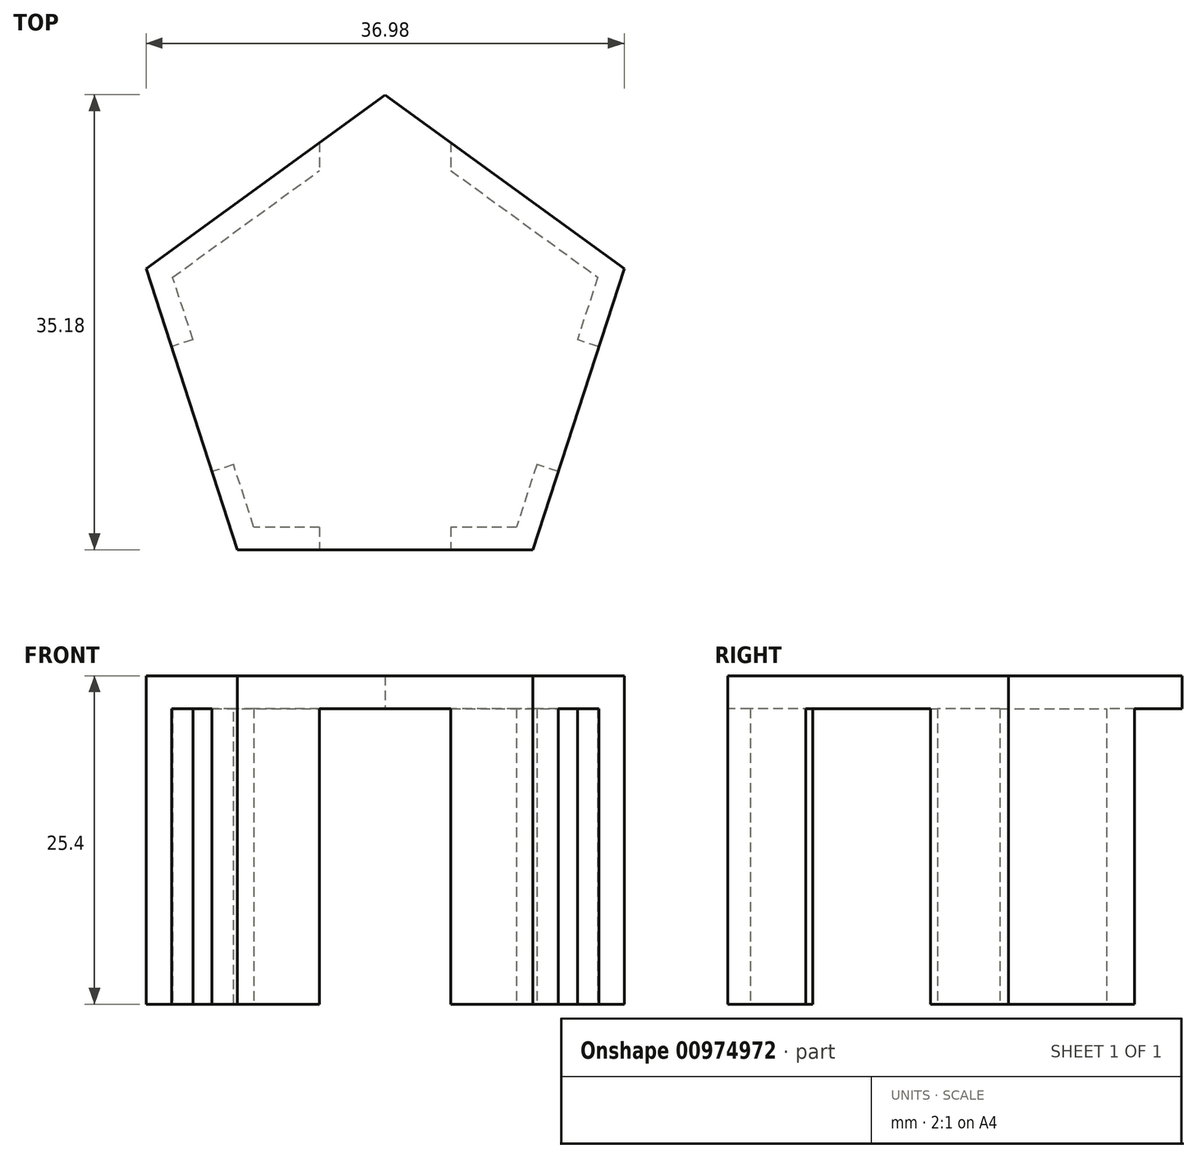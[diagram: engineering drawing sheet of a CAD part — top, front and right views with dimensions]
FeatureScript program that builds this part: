
annotation { "Feature Type Name" : "Feature", "Feature Type Description" : "" }
export const myFeature = defineFeature(function(context is Context, id is Id, definition is map)
    precondition{}
    {
        {
            var Q0;
            Q0=qCreatedBy(makeId("Top.planeOp"),FACE);
            var sketch = newSketch(context, id + "F0", { "sketchPlane" : qUnion([Q0])});
            skCircle(sketch, "E0.cCircle", {"center": v(0, 0) * mm, "radius": 19.45 * mm, "construction": true});
            skLineSegment(sketch, "E0.0", {"start": v(11.43, -15.73) * mm, "end": v(-11.43, -15.73) * mm});
            skLineSegment(sketch, "E0.1", {"start": v(-11.43, -15.73) * mm, "end": v(-18.5, 6) * mm});
            skLineSegment(sketch, "E0.2", {"start": v(-18.5, 6) * mm, "end": v(0, 19.45) * mm});
            skLineSegment(sketch, "E0.3", {"start": v(0, 19.45) * mm, "end": v(18.5, 6) * mm});
            skLineSegment(sketch, "E0.4", {"start": v(18.5, 6) * mm, "end": v(11.43, -15.73) * mm});
            skSolve(sketch);
        }
        {
            var Q0;
            Q0=makeQuery(id+"F0.imprint","IMPRINT",FACE,{"disambiguationData":[TD([[makeQuery(id+"F0.imprint","IMPRINT",EDGE,{"derivedFrom":sQuery(id+"F0.wireOp",EDGE,"E0.0")}),-1.0]])]});
            extrude(context, id + "F1", {"entities" : qUnion([Q0]), "depth" : 25.4 * mm, "offsetDistance" : 25.4 * mm});
        }
        {
            var Q0;
            Q0=qCreatedBy(makeId("Top.planeOp"),FACE);
            var sketch = newSketch(context, id + "F2", { "sketchPlane" : qUnion([Q0])});
            skCircle(sketch, "E1.cCircle", {"center": v(0, 0) * mm, "radius": 13.98 * mm, "construction": true});
            skLineSegment(sketch, "E1.0", {"start": v(16.44, 5.34) * mm, "end": v(10.16, -13.98) * mm});
            skLineSegment(sketch, "E1.1", {"start": v(10.16, -13.98) * mm, "end": v(-10.16, -13.98) * mm});
            skLineSegment(sketch, "E1.2", {"start": v(-10.16, -13.98) * mm, "end": v(-16.44, 5.34) * mm});
            skLineSegment(sketch, "E1.3", {"start": v(-16.44, 5.34) * mm, "end": v(0, 17.29) * mm});
            skLineSegment(sketch, "E1.4", {"start": v(0, 17.29) * mm, "end": v(16.44, 5.34) * mm});
            skPoint(sketch, "E1.0.midPoint", {"position": v(13.3, -4.32) * mm});
            skSolve(sketch);
        }
        {
            var Q0;
            Q0 = qSketchRegion(id + "F2", true);
            extrude(context, id + "F3", {"entities" : qUnion([Q0]), "operationType" : NewBodyOperationType.REMOVE, "depth" : 22.86 * mm, "offsetDistance" : 25.4 * mm});
        }
        {
            var Q0;
            Q0=makeQuery(id+"F1.opExtrude","CAP_FACE",FACE,{"disambiguationData":[OSD([sQuery(id+"F0.wireOp",EDGE,"E0.0"),sQuery(id+"F0.wireOp",EDGE,"E0.1"),sQuery(id+"F0.wireOp",EDGE,"E0.2"),sQuery(id+"F0.wireOp",EDGE,"E0.3"),sQuery(id+"F0.wireOp",EDGE,"E0.4")])],"isStart":true});
            var sketch = newSketch(context, id + "F4", { "sketchPlane" : qUnion([Q0])});
            skLineSegment(sketch, "E2", {"start": v(0, 0) * mm, "end": v(23.62, 7.67) * mm});
            skLineSegment(sketch, "E3", {"start": v(0, 0) * mm, "end": v(-35.57, 11.56) * mm});
            skLineSegment(sketch, "E4", {"start": v(0, 0) * mm, "end": v(0, -28.1) * mm});
            skLineSegment(sketch, "E5.bottom", {"start": v(-11.25, -1.69) * mm, "end": v(-18.5, 0.67) * mm});
            skLineSegment(sketch, "E5.top", {"start": v(-8.1, 7.98) * mm, "end": v(-15.35, 10.33) * mm});
            skLineSegment(sketch, "E5.left", {"start": v(-11.25, -1.69) * mm, "end": v(-8.1, 7.98) * mm});
            skLineSegment(sketch, "E5.right", {"start": v(-18.5, 0.67) * mm, "end": v(-15.35, 10.33) * mm});
            skPoint(sketch, "E5.middle", {"position": v(-13.3, 4.32) * mm});
            skLineSegment(sketch, "E6.bottom", {"start": v(18.5, 0.67) * mm, "end": v(11.25, -1.69) * mm});
            skLineSegment(sketch, "E6.top", {"start": v(15.35, 10.33) * mm, "end": v(8.1, 7.98) * mm});
            skLineSegment(sketch, "E6.left", {"start": v(18.5, 0.67) * mm, "end": v(15.35, 10.33) * mm});
            skLineSegment(sketch, "E6.right", {"start": v(11.25, -1.69) * mm, "end": v(8.1, 7.98) * mm});
            skPoint(sketch, "E6.middle", {"position": v(13.3, 4.32) * mm});
            skLineSegment(sketch, "E7.bottom", {"start": v(5.08, -22.37) * mm, "end": v(-5.08, -22.37) * mm});
            skLineSegment(sketch, "E7.top", {"start": v(5.08, -12.2) * mm, "end": v(-5.08, -12.2) * mm});
            skLineSegment(sketch, "E7.left", {"start": v(5.08, -22.37) * mm, "end": v(5.08, -12.2) * mm});
            skLineSegment(sketch, "E7.right", {"start": v(-5.08, -22.37) * mm, "end": v(-5.08, -12.2) * mm});
            skPoint(sketch, "E7.middle", {"position": v(0, -17.29) * mm});
            skLineSegment(sketch, "E8.bottom", {"start": v(5.08, 10.17) * mm, "end": v(-5.08, 10.17) * mm});
            skLineSegment(sketch, "E8.top", {"start": v(5.08, 17.8) * mm, "end": v(-5.08, 17.8) * mm});
            skLineSegment(sketch, "E8.left", {"start": v(5.08, 10.17) * mm, "end": v(5.08, 17.8) * mm});
            skLineSegment(sketch, "E8.right", {"start": v(-5.08, 10.17) * mm, "end": v(-5.08, 17.8) * mm});
            skPoint(sketch, "E8.middle", {"position": v(0, 13.98) * mm});
            skSolve(sketch);
        }
        {
            var Q0;
            {var subQ0=sQuery(id+"F4.wireOp",EDGE,"E3");var subQ1=makeQuery(id+"F3.boolean.opBoolean","COPY",EDGE,{"derivedFrom":makeQuery(id+"F3.opExtrude","CAP_EDGE",EDGE,{"disambiguationData":[OSD([sQuery(id+"F2.wireOp",EDGE,"E1.2")])],"isStart":true})});var subQ2=makeQuery(id+"F4.imprint","INTERSECT",VERTEX,{"derivedFrom":[subQ1,subQ0]});Q0=makeQuery(id+"F4.imprint","IMPRINT",FACE,{"disambiguationData":[TD([[makeQuery(id+"F4.imprint","IMPRINT",EDGE,{"disambiguationData":[TD([[subQ2,-1.0]])],"derivedFrom":subQ0}),1.0]])]});}
            var Q1;
            {var subQ0=sQuery(id+"F4.wireOp",EDGE,"E3");var subQ1=makeQuery(id+"F3.boolean.opBoolean","COPY",EDGE,{"derivedFrom":makeQuery(id+"F3.opExtrude","CAP_EDGE",EDGE,{"disambiguationData":[OSD([sQuery(id+"F2.wireOp",EDGE,"E1.2")])],"isStart":true})});var subQ2=makeQuery(id+"F4.imprint","INTERSECT",VERTEX,{"derivedFrom":[subQ1,subQ0]});Q1=makeQuery(id+"F4.imprint","IMPRINT",FACE,{"disambiguationData":[TD([[makeQuery(id+"F4.imprint","IMPRINT",EDGE,{"disambiguationData":[TD([[subQ2,-1.0]])],"derivedFrom":subQ0}),-1.0]])]});}
            var Q2;
            {var subQ0=sQuery(id+"F4.wireOp",EDGE,"E2");var subQ1=makeQuery(id+"F3.boolean.opBoolean","COPY",EDGE,{"derivedFrom":makeQuery(id+"F3.opExtrude","CAP_EDGE",EDGE,{"disambiguationData":[OSD([sQuery(id+"F2.wireOp",EDGE,"E1.0")])],"isStart":true})});var subQ2=makeQuery(id+"F4.imprint","INTERSECT",VERTEX,{"derivedFrom":[subQ1,subQ0]});Q2=makeQuery(id+"F4.imprint","IMPRINT",FACE,{"disambiguationData":[TD([[makeQuery(id+"F4.imprint","IMPRINT",EDGE,{"disambiguationData":[TD([[subQ2,-1.0]])],"derivedFrom":subQ0}),1.0]])]});}
            var Q3;
            {var subQ0=sQuery(id+"F4.wireOp",EDGE,"E2");var subQ1=makeQuery(id+"F3.boolean.opBoolean","COPY",EDGE,{"derivedFrom":makeQuery(id+"F3.opExtrude","CAP_EDGE",EDGE,{"disambiguationData":[OSD([sQuery(id+"F2.wireOp",EDGE,"E1.0")])],"isStart":true})});var subQ2=makeQuery(id+"F4.imprint","INTERSECT",VERTEX,{"derivedFrom":[subQ1,subQ0]});Q3=makeQuery(id+"F4.imprint","IMPRINT",FACE,{"disambiguationData":[TD([[makeQuery(id+"F4.imprint","IMPRINT",EDGE,{"disambiguationData":[TD([[subQ2,-1.0]])],"derivedFrom":subQ0}),-1.0]])]});}
            var Q4;
            {var subQ1=makeQuery(id+"F1.opExtrude","CAP_EDGE",EDGE,{"disambiguationData":[OSD([sQuery(id+"F0.wireOp",EDGE,"E0.2")])],"isStart":true});var subQ5=sQuery(id+"F4.wireOp",EDGE,"E7.right");var subQ6=makeQuery(id+"F4.imprint","INTERSECT",VERTEX,{"derivedFrom":[subQ1,subQ5]});Q4=makeQuery(id+"F4.imprint","IMPRINT",FACE,{"disambiguationData":[TD([[makeQuery(id+"F4.imprint","IMPRINT",EDGE,{"disambiguationData":[TD([[subQ6,-1.0]])],"derivedFrom":subQ5}),-1.0]])]});}
            var Q5;
            {var subQ1=makeQuery(id+"F1.opExtrude","CAP_EDGE",EDGE,{"disambiguationData":[OSD([sQuery(id+"F0.wireOp",EDGE,"E0.3")])],"isStart":true});var subQ5=sQuery(id+"F4.wireOp",EDGE,"E7.left");var subQ6=makeQuery(id+"F4.imprint","INTERSECT",VERTEX,{"derivedFrom":[subQ1,subQ5]});Q5=makeQuery(id+"F4.imprint","IMPRINT",FACE,{"disambiguationData":[TD([[makeQuery(id+"F4.imprint","IMPRINT",EDGE,{"disambiguationData":[TD([[subQ6,-1.0]])],"derivedFrom":subQ5}),1.0]])]});}
            var Q6;
            {var subQ0=sQuery(id+"F4.wireOp",EDGE,"E8.left");var subQ1=makeQuery(id+"F1.opExtrude","CAP_EDGE",EDGE,{"disambiguationData":[OSD([sQuery(id+"F0.wireOp",EDGE,"E0.0")])],"isStart":true});var subQ2=makeQuery(id+"F4.imprint","INTERSECT",VERTEX,{"derivedFrom":[subQ1,subQ0]});Q6=makeQuery(id+"F4.imprint","IMPRINT",FACE,{"disambiguationData":[TD([[makeQuery(id+"F4.imprint","IMPRINT",EDGE,{"disambiguationData":[TD([[subQ2,1.0]])],"derivedFrom":subQ0}),1.0]])]});}
            extrude(context, id + "F5", {"entities" : qUnion([Q0, Q1, Q2, Q3, Q4, Q5, Q6]), "operationType" : NewBodyOperationType.REMOVE, "oppositeDirection" : true, "depth" : 22.86 * mm, "offsetDistance" : 25.4 * mm});
        }
    });
